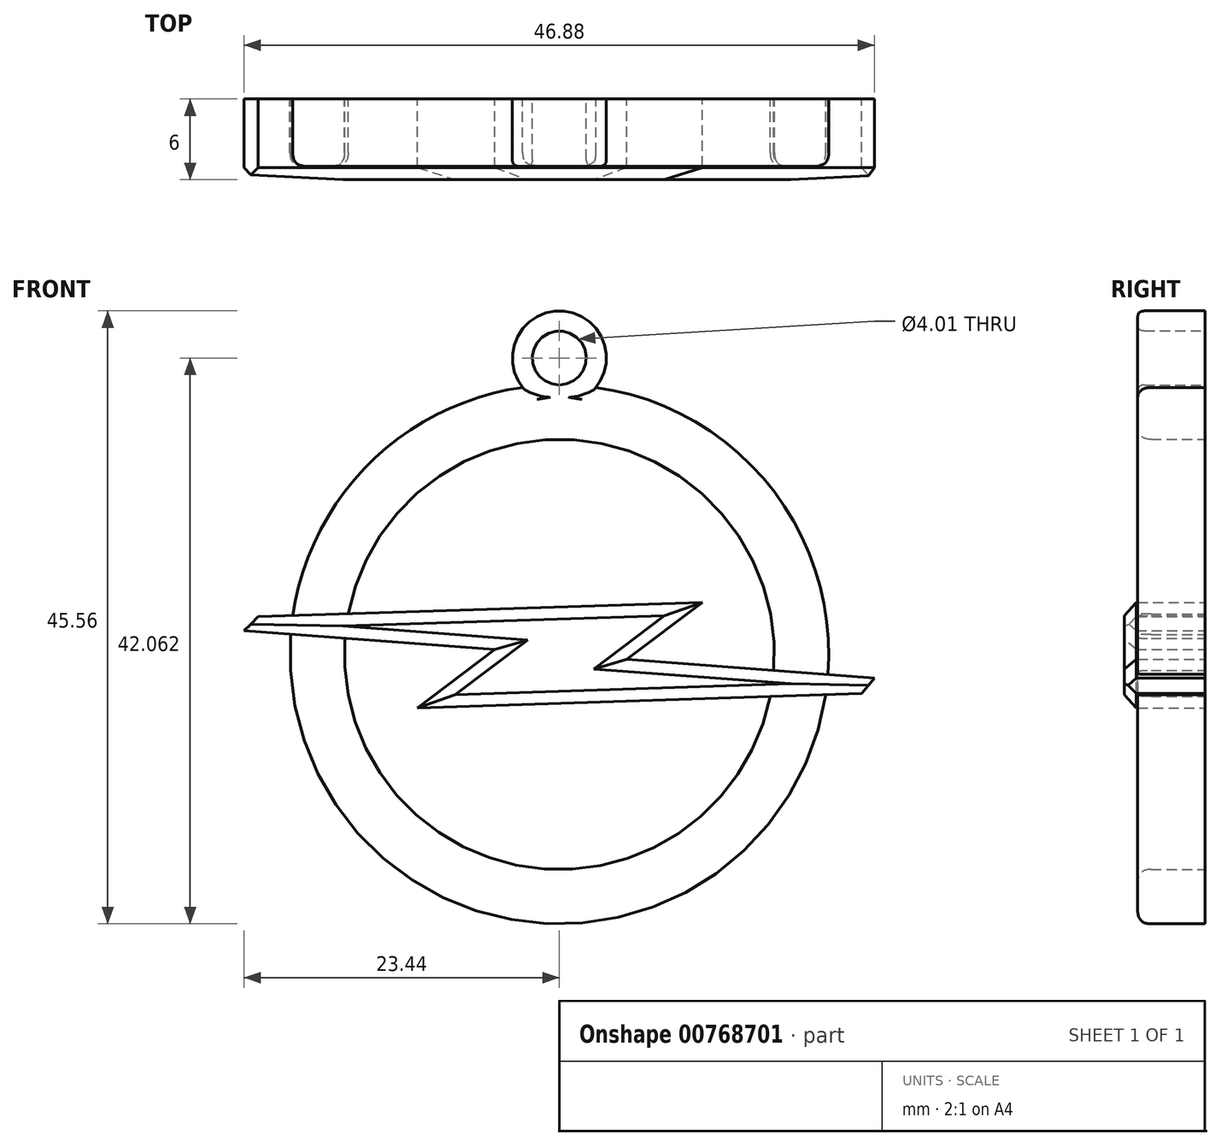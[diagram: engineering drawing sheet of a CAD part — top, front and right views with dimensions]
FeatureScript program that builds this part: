
annotation { "Feature Type Name" : "Feature", "Feature Type Description" : "" }
export const myFeature = defineFeature(function(context is Context, id is Id, definition is map)
    precondition{}
    {
        {
            var Q0;
            Q0=qCreatedBy(makeId("Front.planeOp"),FACE);
            var sketch = newSketch(context, id + "F0", { "sketchPlane" : qUnion([Q0])});
            skCircle(sketch, "E0", {"center": v(0, 0) * mm, "radius": 20.03 * mm});
            skCircle(sketch, "E1", {"center": v(0, 0) * mm, "radius": 15.98 * mm});
            skCircle(sketch, "E2", {"center": v(0, 22.03) * mm, "radius": 2 * mm});
            skCircle(sketch, "E3", {"center": v(0, 22.03) * mm, "radius": 3.5 * mm});
            skLineSegment(sketch, "E4", {"start": v(-23.44, 1.75) * mm, "end": v(-22.38, 2.8) * mm});
            skLineSegment(sketch, "E5", {"start": v(-22.38, 2.8) * mm, "end": v(10.61, 3.86) * mm});
            skLineSegment(sketch, "E6", {"start": v(10.61, 3.86) * mm, "end": v(5.01, -0.37) * mm});
            skLineSegment(sketch, "E7", {"start": v(23.44, -1.75) * mm, "end": v(22.48, -2.92) * mm});
            skLineSegment(sketch, "E8", {"start": v(22.48, -2.92) * mm, "end": v(-10.54, -3.98) * mm});
            skLineSegment(sketch, "E9", {"start": v(-10.54, -3.98) * mm, "end": v(-4.8, 0.36) * mm});
            skLineSegment(sketch, "E10", {"start": v(5.01, -0.37) * mm, "end": v(23.44, -1.75) * mm});
            skLineSegment(sketch, "E11", {"start": v(-4.8, 0.36) * mm, "end": v(-23.44, 1.75) * mm});
            skSolve(sketch);
        }
        {
            var Q0;
            {var subQ0=sQuery(id+"F0.wireOp",EDGE,"E2");Q0=makeQuery(id+"F0.imprint","IMPRINT",FACE,{"disambiguationData":[TD([[makeQuery(id+"F0.imprint","IMPRINT",EDGE,{"derivedFrom":subQ0}),-1.0]])]});}
            var Q1;
            {var subQ5=sQuery(id+"F0.wireOp",EDGE,"E3");var subQ6=sQuery(id+"F0.wireOp",EDGE,"E0");var subQ9=makeQuery(id+"F0.imprint","INTERSECT",VERTEX,{"disambiguationData":[OD(1.0)],"derivedFrom":[subQ6,subQ5]});Q1=makeQuery(id+"F0.imprint","IMPRINT",FACE,{"disambiguationData":[TD([[makeQuery(id+"F0.imprint","IMPRINT",EDGE,{"disambiguationData":[TD([[subQ9,-1.0]])],"derivedFrom":subQ6}),1.0]])]});}
            var Q2;
            {var subQ0=sQuery(id+"F0.wireOp",EDGE,"E0");var subQ1=makeQuery(id+"F0.imprint","INTERSECT",VERTEX,{"derivedFrom":[subQ0,sQuery(id+"F0.wireOp",EDGE,"E2")]});Q2=makeQuery(id+"F0.imprint","IMPRINT",FACE,{"disambiguationData":[TD([[makeQuery(id+"F0.imprint","IMPRINT",EDGE,{"disambiguationData":[TD([[subQ1,1.0]])],"derivedFrom":subQ0}),1.0]])]});}
            var Q3;
            {var subQ0=sQuery(id+"F0.wireOp",EDGE,"E11");var subQ1=sQuery(id+"F0.wireOp",EDGE,"E0");var subQ2=makeQuery(id+"F0.imprint","INTERSECT",VERTEX,{"derivedFrom":[subQ1,subQ0]});Q3=makeQuery(id+"F0.imprint","IMPRINT",FACE,{"disambiguationData":[TD([[makeQuery(id+"F0.imprint","IMPRINT",EDGE,{"disambiguationData":[TD([[subQ2,-1.0]])],"derivedFrom":subQ1}),1.0]])]});}
            extrude(context, id + "F1", {"entities" : qUnion([Q0, Q1, Q2, Q3]), "depth" : 5 * mm, "offsetDistance" : 25 * mm});
        }
        {
            var Q0;
            {var subQ0=sQuery(id+"F0.wireOp",EDGE,"E0");Q0=makeQuery(id+"F1.opExtrude","CAP_EDGE",EDGE,{"disambiguationData":[OSD([subQ0]),TDD([makeQuery(id+"F0.imprint","IMPRINT",EDGE,{"disambiguationData":[TD([[makeQuery(id+"F0.imprint","INTERSECT",VERTEX,{"disambiguationData":[OD(1.0)],"derivedFrom":[subQ0,sQuery(id+"F0.wireOp",EDGE,"E3")]}),-1.0]])],"derivedFrom":subQ0})])],"isStart":false});}
            var Q1;
            {var subQ0=sQuery(id+"F0.wireOp",EDGE,"E1");Q1=makeQuery(id+"F1.opExtrude","CAP_EDGE",EDGE,{"disambiguationData":[OSD([subQ0]),TDD([makeQuery(id+"F0.imprint","IMPRINT",EDGE,{"disambiguationData":[TD([[makeQuery(id+"F0.imprint","INTERSECT",VERTEX,{"derivedFrom":[subQ0,sQuery(id+"F0.wireOp",EDGE,"E5")]}),1.0]])],"derivedFrom":subQ0})])],"isStart":false});}
            var Q2;
            {var subQ0=sQuery(id+"F0.wireOp",EDGE,"E0");Q2=makeQuery(id+"F1.opExtrude","CAP_EDGE",EDGE,{"disambiguationData":[OSD([subQ0]),TDD([makeQuery(id+"F0.imprint","IMPRINT",EDGE,{"disambiguationData":[TD([[makeQuery(id+"F0.imprint","INTERSECT",VERTEX,{"disambiguationData":[OD(0.0)],"derivedFrom":[subQ0,sQuery(id+"F0.wireOp",EDGE,"E3")]}),1.0]])],"derivedFrom":subQ0})])],"isStart":false});}
            var Q3;
            {var subQ0=sQuery(id+"F0.wireOp",EDGE,"E1");Q3=makeQuery(id+"F1.opExtrude","CAP_EDGE",EDGE,{"disambiguationData":[OSD([subQ0]),TDD([makeQuery(id+"F0.imprint","IMPRINT",EDGE,{"disambiguationData":[TD([[makeQuery(id+"F0.imprint","INTERSECT",VERTEX,{"derivedFrom":[subQ0,sQuery(id+"F0.wireOp",EDGE,"E11")]}),-1.0]])],"derivedFrom":subQ0})])],"isStart":false});}
            var Q4;
            {var subQ0=sQuery(id+"F0.wireOp",EDGE,"E0");Q4=makeQuery(id+"F1.opExtrude","CAP_EDGE",EDGE,{"disambiguationData":[OSD([subQ0]),TDD([makeQuery(id+"F0.imprint","IMPRINT",EDGE,{"disambiguationData":[TD([[makeQuery(id+"F0.imprint","INTERSECT",VERTEX,{"derivedFrom":[subQ0,sQuery(id+"F0.wireOp",EDGE,"E11")]}),-1.0]])],"derivedFrom":subQ0})])],"isStart":false});}
            fillet(context, id + "F2", {"entities" : qUnion([Q0, Q1, Q2, Q3, Q4]), "radius" : 1 * mm, "tangentPropagation" : true, "rho" : 0.5, "crossSection" : FilletCrossSection.CONIC, "allowEdgeOverflow" : false});
        }
        {
            var Q0;
            Q0=makeQuery(id+"F1.opExtrude","CAP_EDGE",EDGE,{"disambiguationData":[OSD([sQuery(id+"F0.wireOp",EDGE,"E3")])],"isStart":false});
            var Q1;
            Q1=makeQuery(id+"F1.opExtrude","CAP_EDGE",EDGE,{"disambiguationData":[OSD([sQuery(id+"F0.wireOp",EDGE,"E2")])],"isStart":false});
            fillet(context, id + "F3", {"entities" : qUnion([Q0, Q1]), "radius" : 0.5 * mm, "tangentPropagation" : true, "rho" : 0.5, "crossSection" : FilletCrossSection.CONIC, "allowEdgeOverflow" : false});
        }
        {
            var Q0;
            {var subQ0=sQuery(id+"F0.wireOp",EDGE,"E6");Q0=makeQuery(id+"F0.imprint","IMPRINT",FACE,{"disambiguationData":[TD([[makeQuery(id+"F0.imprint","IMPRINT",EDGE,{"derivedFrom":subQ0}),-1.0]])]});}
            var Q1;
            {var subQ0=sQuery(id+"F0.wireOp",EDGE,"E5");var subQ1=sQuery(id+"F0.wireOp",EDGE,"E0");var subQ2=makeQuery(id+"F0.imprint","INTERSECT",VERTEX,{"derivedFrom":[subQ1,subQ0]});Q1=makeQuery(id+"F0.imprint","IMPRINT",FACE,{"disambiguationData":[TD([[makeQuery(id+"F0.imprint","IMPRINT",EDGE,{"disambiguationData":[TD([[subQ2,-1.0]])],"derivedFrom":subQ1}),1.0]])]});}
            var Q2;
            {var subQ5=sQuery(id+"F0.wireOp",EDGE,"E4");Q2=makeQuery(id+"F0.imprint","IMPRINT",FACE,{"disambiguationData":[TD([[makeQuery(id+"F0.imprint","IMPRINT",EDGE,{"derivedFrom":subQ5}),-1.0]])]});}
            var Q3;
            {var subQ0=sQuery(id+"F0.wireOp",EDGE,"E8");var subQ1=sQuery(id+"F0.wireOp",EDGE,"E0");var subQ2=makeQuery(id+"F0.imprint","INTERSECT",VERTEX,{"derivedFrom":[subQ1,subQ0]});Q3=makeQuery(id+"F0.imprint","IMPRINT",FACE,{"disambiguationData":[TD([[makeQuery(id+"F0.imprint","IMPRINT",EDGE,{"disambiguationData":[TD([[subQ2,-1.0]])],"derivedFrom":subQ1}),1.0]])]});}
            var Q4;
            {var subQ5=sQuery(id+"F0.wireOp",EDGE,"E7");Q4=makeQuery(id+"F0.imprint","IMPRINT",FACE,{"disambiguationData":[TD([[makeQuery(id+"F0.imprint","IMPRINT",EDGE,{"derivedFrom":subQ5}),-1.0]])]});}
            extrude(context, id + "F4", {"entities" : qUnion([Q0, Q1, Q2, Q3, Q4]), "depth" : 6 * mm, "offsetDistance" : 25 * mm});
        }
        {
            var Q0;
            Q0=makeQuery(id+"F4.opExtrude","CAP_EDGE",EDGE,{"disambiguationData":[OSD([sQuery(id+"F0.wireOp",EDGE,"E5")])],"isStart":false});
            var Q1;
            Q1=makeQuery(id+"F4.opExtrude","CAP_EDGE",EDGE,{"disambiguationData":[OSD([sQuery(id+"F0.wireOp",EDGE,"E11")])],"isStart":false});
            var Q2;
            Q2=makeQuery(id+"F4.opExtrude","CAP_EDGE",EDGE,{"disambiguationData":[OSD([sQuery(id+"F0.wireOp",EDGE,"E8")])],"isStart":false});
            var Q3;
            Q3=makeQuery(id+"F4.opExtrude","CAP_EDGE",EDGE,{"disambiguationData":[OSD([sQuery(id+"F0.wireOp",EDGE,"E9")])],"isStart":false});
            var Q4;
            Q4=makeQuery(id+"F4.opExtrude","CAP_EDGE",EDGE,{"disambiguationData":[OSD([sQuery(id+"F0.wireOp",EDGE,"E6")])],"isStart":false});
            var Q5;
            Q5=makeQuery(id+"F4.opExtrude","CAP_EDGE",EDGE,{"disambiguationData":[OSD([sQuery(id+"F0.wireOp",EDGE,"E10")])],"isStart":false});
            chamfer(context, id + "F5", {"entities" : qUnion([Q0, Q1, Q2, Q3, Q4, Q5]), "width" : 0.9 * mm});
        }
    });
